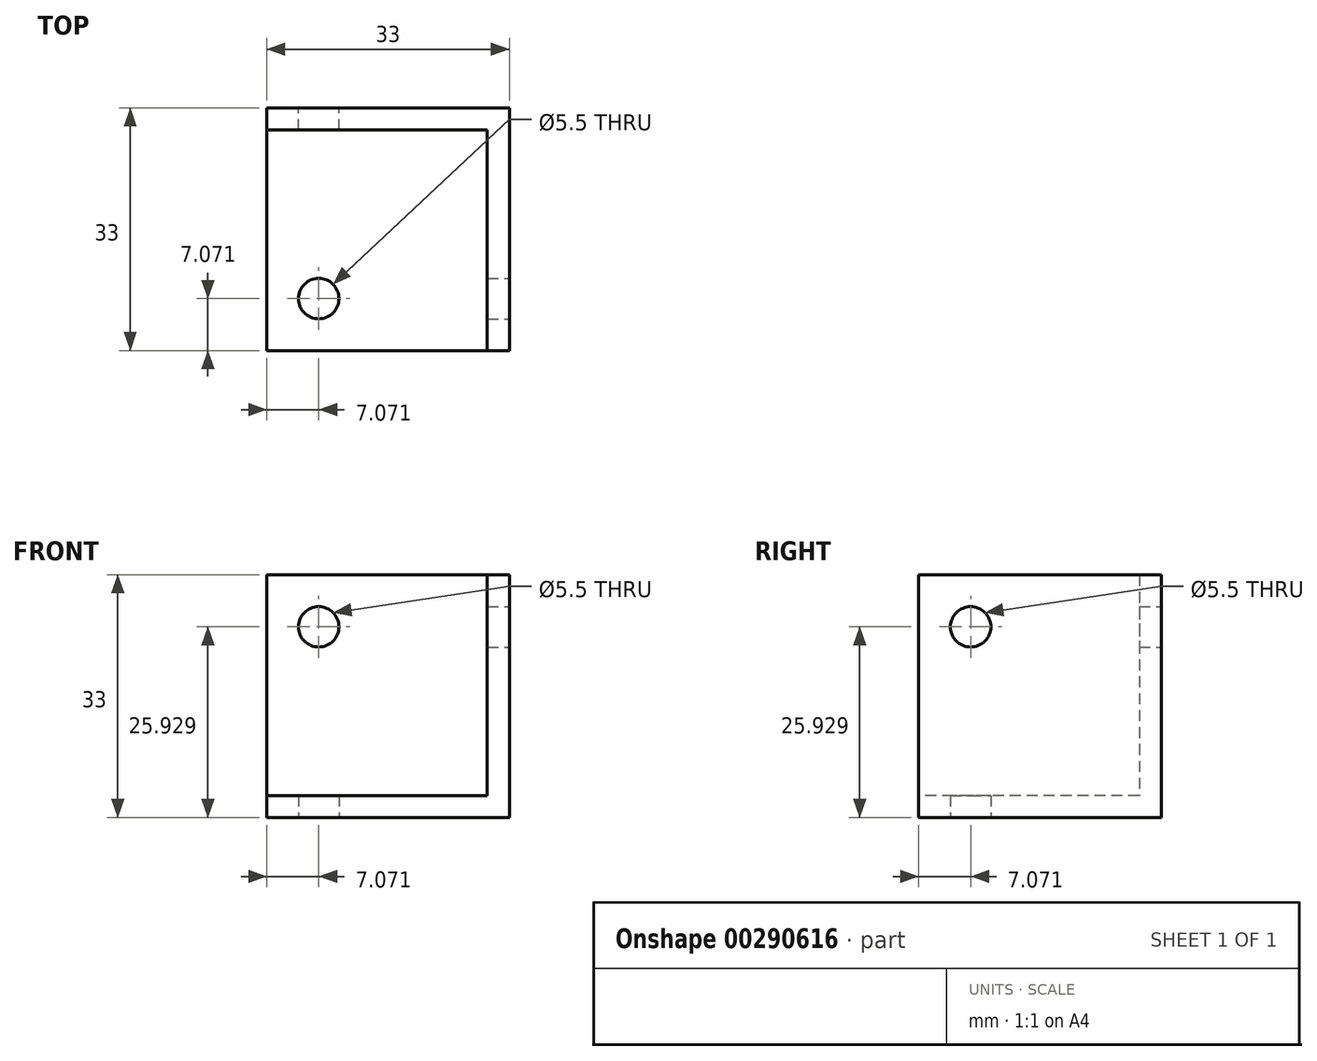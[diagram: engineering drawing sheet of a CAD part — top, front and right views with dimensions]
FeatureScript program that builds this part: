
annotation { "Feature Type Name" : "Feature", "Feature Type Description" : "" }
export const myFeature = defineFeature(function(context is Context, id is Id, definition is map)
    precondition{}
    {
        {
            var Q0;
            Q0=qCreatedBy(makeId("Top.planeOp"),FACE);
            var sketch = newSketch(context, id + "F0", { "sketchPlane" : qUnion([Q0])});
            skLineSegment(sketch, "E0.bottom", {"start": v(-16.5, 16.5) * mm, "end": v(16.5, 16.5) * mm});
            skLineSegment(sketch, "E0.top", {"start": v(-16.5, -16.5) * mm, "end": v(16.5, -16.5) * mm});
            skLineSegment(sketch, "E0.left", {"start": v(-16.5, 16.5) * mm, "end": v(-16.5, -16.5) * mm});
            skLineSegment(sketch, "E0.right", {"start": v(16.5, 16.5) * mm, "end": v(16.5, -16.5) * mm});
            skLineSegment(sketch, "E1", {"start": v(0, 16.5) * mm, "end": v(0, -16.5) * mm, "construction": true});
            skSolve(sketch);
        }
        {
            var Q0;
            Q0 = qSketchRegion(id + "F0", true);
            extrude(context, id + "F1", {"entities" : qUnion([Q0]), "depth" : 3 * mm});
        }
        {
            var Q0;
            Q0=makeQuery(id+"F1.opExtrude","CAP_FACE",FACE,{"disambiguationData":[OSD([sQuery(id+"F0.wireOp",EDGE,"E0.bottom"),sQuery(id+"F0.wireOp",EDGE,"E0.top"),sQuery(id+"F0.wireOp",EDGE,"E0.left"),sQuery(id+"F0.wireOp",EDGE,"E0.right")])],"isStart":false});
            var sketch = newSketch(context, id + "F2", { "sketchPlane" : qUnion([Q0])});
            skLineSegment(sketch, "E2.bottom", {"start": v(-16.5, 16.5) * mm, "end": v(16.5, 16.5) * mm});
            skLineSegment(sketch, "E2.top", {"start": v(-16.5, 13.5) * mm, "end": v(16.5, 13.5) * mm});
            skLineSegment(sketch, "E2.left", {"start": v(-16.5, 16.5) * mm, "end": v(-16.5, 13.5) * mm});
            skLineSegment(sketch, "E2.right", {"start": v(16.5, 16.5) * mm, "end": v(16.5, 13.5) * mm});
            skLineSegment(sketch, "E3.bottom", {"start": v(16.5, 16.5) * mm, "end": v(13.5, 16.5) * mm});
            skLineSegment(sketch, "E3.top", {"start": v(16.5, -16.5) * mm, "end": v(13.5, -16.5) * mm});
            skLineSegment(sketch, "E3.left", {"start": v(16.5, 16.5) * mm, "end": v(16.5, -16.5) * mm});
            skLineSegment(sketch, "E3.right", {"start": v(13.5, 16.5) * mm, "end": v(13.5, -16.5) * mm});
            skSolve(sketch);
        }
        {
            var Q0;
            Q0 = qSketchRegion(id + "F2", true);
            extrude(context, id + "F3", {"entities" : qUnion([Q0]), "operationType" : NewBodyOperationType.ADD, "depth" : 30 * mm});
        }
        {
            var Q0;
            Q0=makeQuery(id+"F1.opExtrude","CAP_FACE",FACE,{"disambiguationData":[OSD([sQuery(id+"F0.wireOp",EDGE,"E0.bottom"),sQuery(id+"F0.wireOp",EDGE,"E0.top"),sQuery(id+"F0.wireOp",EDGE,"E0.left"),sQuery(id+"F0.wireOp",EDGE,"E0.right")])],"isStart":true});
            var sketch = newSketch(context, id + "F4", { "sketchPlane" : qUnion([Q0])});
            skLineSegment(sketch, "E4", {"start": v(-16.5, 16.5) * mm, "end": v(16.5, -16.5) * mm, "construction": true});
            skCircle(sketch, "E5", {"center": v(-9.43, 9.43) * mm, "radius": 2.75 * mm});
            skSolve(sketch);
        }
        {
            var Q0;
            Q0=makeQuery(id+"F3.boolean.opBoolean","MERGE",FACE,{"derivedFrom":[makeQuery(id+"F1.opExtrude","SWEPT_FACE",FACE,{"disambiguationData":[OSD([sQuery(id+"F0.wireOp",EDGE,"E0.right")])]}),makeQuery(id+"F3.opExtrude","SWEPT_FACE",FACE,{"disambiguationData":[OSD([sQuery(id+"F2.wireOp",EDGE,"E3.left")])]})]});
            var sketch = newSketch(context, id + "F5", { "sketchPlane" : qUnion([Q0])});
            skLineSegment(sketch, "E6", {"start": v(16.5, 0) * mm, "end": v(-16.5, 33) * mm, "construction": true});
            skCircle(sketch, "E7", {"center": v(-9.43, 25.93) * mm, "radius": 2.75 * mm});
            skSolve(sketch);
        }
        {
            var Q0;
            Q0=makeQuery(id+"F3.boolean.opBoolean","MERGE",FACE,{"derivedFrom":[makeQuery(id+"F1.opExtrude","SWEPT_FACE",FACE,{"disambiguationData":[OSD([sQuery(id+"F0.wireOp",EDGE,"E0.bottom")])]}),makeQuery(id+"F3.opExtrude","SWEPT_FACE",FACE,{"disambiguationData":[OSD([sQuery(id+"F2.wireOp",EDGE,"E2.bottom"),sQuery(id+"F2.wireOp",EDGE,"E3.bottom")])]})]});
            var sketch = newSketch(context, id + "F6", { "sketchPlane" : qUnion([Q0])});
            skLineSegment(sketch, "E8", {"start": v(-16.5, 0) * mm, "end": v(16.5, 33) * mm, "construction": true});
            skCircle(sketch, "E9", {"center": v(9.43, 25.93) * mm, "radius": 2.75 * mm});
            skSolve(sketch);
        }
        {
            var Q0;
            Q0=makeQuery(id+"F6.imprint","IMPRINT",FACE,{"disambiguationData":[TD([[makeQuery(id+"F6.imprint","IMPRINT",EDGE,{"derivedFrom":sQuery(id+"F6.wireOp",EDGE,"E9")}),1.0]])]});
            extrude(context, id + "F7", {"entities" : qUnion([Q0]), "operationType" : NewBodyOperationType.REMOVE, "oppositeDirection" : true, "depth" : 3 * mm});
        }
        {
            var Q0;
            Q0=makeQuery(id+"F4.imprint","IMPRINT",FACE,{"disambiguationData":[TD([[makeQuery(id+"F4.imprint","IMPRINT",EDGE,{"derivedFrom":sQuery(id+"F4.wireOp",EDGE,"E5")}),1.0]])]});
            extrude(context, id + "F8", {"entities" : qUnion([Q0]), "operationType" : NewBodyOperationType.REMOVE, "oppositeDirection" : true, "depth" : 3 * mm});
        }
        {
            var Q0;
            Q0=makeQuery(id+"F5.imprint","IMPRINT",FACE,{"disambiguationData":[TD([[makeQuery(id+"F5.imprint","IMPRINT",EDGE,{"derivedFrom":sQuery(id+"F5.wireOp",EDGE,"E7")}),1.0]])]});
            extrude(context, id + "F9", {"entities" : qUnion([Q0]), "operationType" : NewBodyOperationType.REMOVE, "oppositeDirection" : true, "depth" : 3 * mm});
        }
    });
